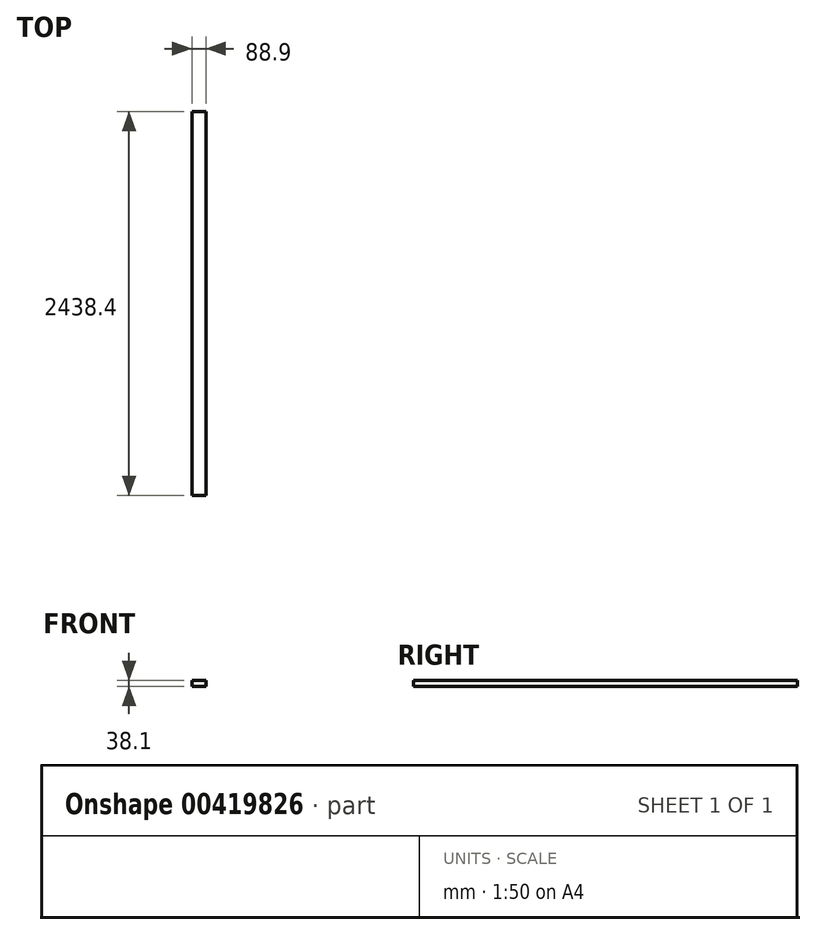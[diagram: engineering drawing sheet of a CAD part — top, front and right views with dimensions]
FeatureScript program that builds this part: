
annotation { "Feature Type Name" : "Feature", "Feature Type Description" : "" }
export const myFeature = defineFeature(function(context is Context, id is Id, definition is map)
    precondition{}
    {
        {
            var Q0;
            Q0=qCreatedBy(makeId("Front.planeOp"),FACE);
            var sketch = newSketch(context, id + "F0", { "sketchPlane" : qUnion([Q0])});
            skLineSegment(sketch, "E0.bottom", {"start": v(0, 0) * mm, "end": v(88.9, 0) * mm});
            skLineSegment(sketch, "E0.top", {"start": v(0, 38.1) * mm, "end": v(88.9, 38.1) * mm});
            skLineSegment(sketch, "E0.left", {"start": v(0, 0) * mm, "end": v(0, 38.1) * mm});
            skLineSegment(sketch, "E0.right", {"start": v(88.9, 0) * mm, "end": v(88.9, 38.1) * mm});
            skSolve(sketch);
        }
        {
            var Q0;
            Q0 = qSketchRegion(id + "F0", true);
            extrude(context, id + "F1", {"entities" : qUnion([Q0]), "depth" : 2438.4 * mm});
        }
    });
